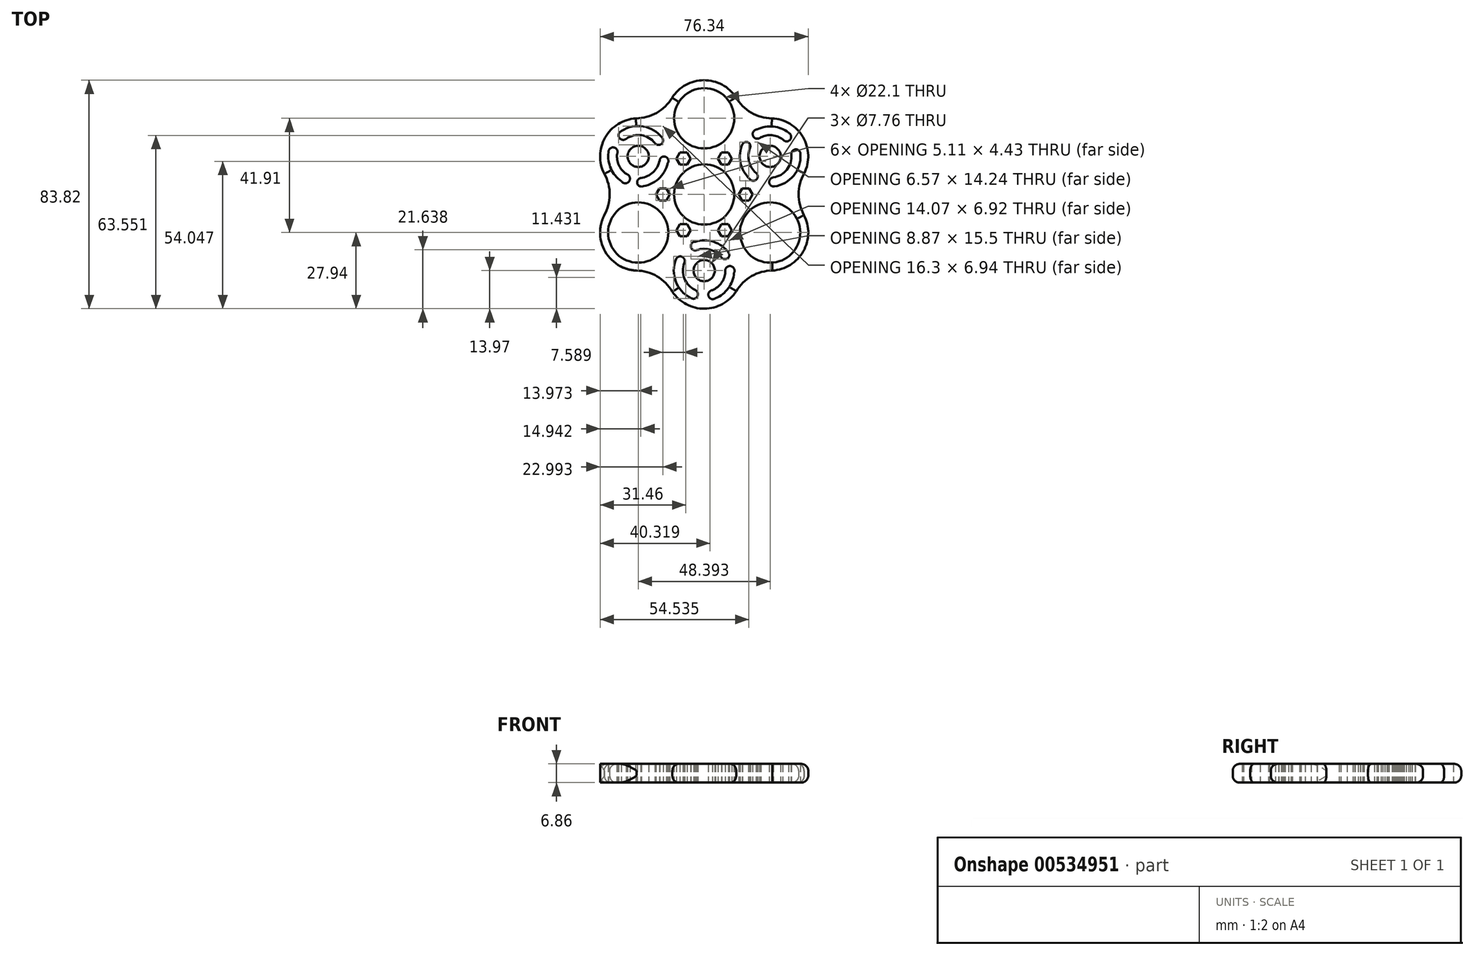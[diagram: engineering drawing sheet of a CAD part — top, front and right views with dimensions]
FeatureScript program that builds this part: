
annotation { "Feature Type Name" : "Feature", "Feature Type Description" : "" }
export const myFeature = defineFeature(function(context is Context, id is Id, definition is map)
    precondition{}
    {
        {
            var Q0;
            Q0=qCreatedBy(makeId("Top.planeOp"),FACE);
            var sketch = newSketch(context, id + "F0", { "sketchPlane" : qUnion([Q0])});
            skCircle(sketch, "E0", {"center": v(0, 0) * mm, "radius": 11.05 * mm});
            skCircle(sketch, "E1", {"center": v(0, 27.94) * mm, "radius": 11.05 * mm});
            skCircle(sketch, "E2.1.0", {"center": v(-24.2, -13.97) * mm, "radius": 11.05 * mm});
            skCircle(sketch, "E2.2.0", {"center": v(24.2, -13.97) * mm, "radius": 11.05 * mm});
            skArc(sketch, "E3", {"start": v(12.1, 34.92) * mm, "mid": v(0.09, 41.9) * mm, "end": v(-12.01, 35.07) * mm});
            skArc(sketch, "E4.1.0", {"start": v(-36.3, -6.98) * mm, "mid": v(-36.34, -20.88) * mm, "end": v(-24.37, -27.94) * mm});
            skArc(sketch, "E4.2.0", {"start": v(24.2, -27.94) * mm, "mid": v(36.25, -21.03) * mm, "end": v(36.38, -7.13) * mm});
            skArc(sketch, "E5.1.0", {"start": v(-24.2, 27.94) * mm, "mid": v(-36.25, 21.03) * mm, "end": v(-36.38, 7.13) * mm});
            skArc(sketch, "E5.3.0", {"start": v(-12.1, -34.92) * mm, "mid": v(-0.09, -41.9) * mm, "end": v(12.01, -35.07) * mm});
            skArc(sketch, "E5.5.0", {"start": v(36.3, 6.98) * mm, "mid": v(36.34, 20.88) * mm, "end": v(24.37, 27.94) * mm});
            skArc(sketch, "E6", {"start": v(-25.03, 27.92) * mm, "mid": v(-17.4, 29.95) * mm, "end": v(-11.76, 35.48) * mm});
            skArc(sketch, "E7.1.0", {"start": v(-36.69, -7.72) * mm, "mid": v(-34.64, -0.1) * mm, "end": v(-36.6, 7.55) * mm});
            skArc(sketch, "E7.2.0", {"start": v(-11.66, -35.63) * mm, "mid": v(-17.23, -30.04) * mm, "end": v(-24.84, -27.93) * mm});
            skArc(sketch, "E7.3.0", {"start": v(25.03, -27.92) * mm, "mid": v(17.4, -29.95) * mm, "end": v(11.76, -35.48) * mm});
            skArc(sketch, "E7.4.0", {"start": v(36.69, 7.72) * mm, "mid": v(34.64, 0.1) * mm, "end": v(36.6, -7.55) * mm});
            skArc(sketch, "E7.5.0", {"start": v(11.66, 35.63) * mm, "mid": v(17.23, 30.04) * mm, "end": v(24.84, 27.93) * mm});
            skCircle(sketch, "E8", {"center": v(-24.2, 13.97) * mm, "radius": 3.88 * mm});
            skArc(sketch, "E9", {"start": v(-15.41, 20.83) * mm, "mid": v(-22.4, 24.97) * mm, "end": v(-30.34, 23.27) * mm});
            skArc(sketch, "E10", {"start": v(-18.06, 18.84) * mm, "mid": v(-23.04, 21.71) * mm, "end": v(-28.64, 20.42) * mm});
            skArc(sketch, "E11", {"start": v(-18.06, 18.84) * mm, "mid": v(-15.73, 18.48) * mm, "end": v(-15.41, 20.83) * mm});
            skArc(sketch, "E12", {"start": v(-30.34, 23.27) * mm, "mid": v(-31.15, 20.85) * mm, "end": v(-28.64, 20.42) * mm});
            skArc(sketch, "E13.1.0", {"start": v(-10.33, -23.76) * mm, "mid": v(-10.42, -31.88) * mm, "end": v(-4.98, -37.9) * mm});
            skArc(sketch, "E13.1.1", {"start": v(-7.28, -25.06) * mm, "mid": v(-7.28, -30.81) * mm, "end": v(-3.36, -35.01) * mm});
            skArc(sketch, "E13.1.2", {"start": v(-7.28, -25.06) * mm, "mid": v(-8.14, -22.86) * mm, "end": v(-10.33, -23.76) * mm});
            skArc(sketch, "E13.1.3", {"start": v(-4.98, -37.9) * mm, "mid": v(-2.48, -37.4) * mm, "end": v(-3.36, -35.01) * mm});
            skArc(sketch, "E13.2.0", {"start": v(25.74, 2.93) * mm, "mid": v(32.82, 6.91) * mm, "end": v(35.32, 14.64) * mm});
            skArc(sketch, "E13.2.1", {"start": v(25.34, 6.22) * mm, "mid": v(30.33, 9.1) * mm, "end": v(32, 14.6) * mm});
            skArc(sketch, "E13.2.2", {"start": v(25.34, 6.22) * mm, "mid": v(23.87, 4.38) * mm, "end": v(25.74, 2.93) * mm});
            skArc(sketch, "E13.2.3", {"start": v(35.32, 14.64) * mm, "mid": v(33.64, 16.55) * mm, "end": v(32, 14.6) * mm});
            skArc(sketch, "E14", {"start": v(-13.35, 11.48) * mm, "mid": v(-16.82, 5.64) * mm, "end": v(-23.02, 2.9) * mm});
            skArc(sketch, "E15", {"start": v(-16.34, 12.55) * mm, "mid": v(-18.73, 8.15) * mm, "end": v(-23.28, 6.04) * mm});
            skArc(sketch, "E16", {"start": v(-30.43, 4.93) * mm, "mid": v(-34.24, 9.53) * mm, "end": v(-35.08, 15.45) * mm});
            skArc(sketch, "E17", {"start": v(-28.52, 7.5) * mm, "mid": v(-31.27, 10.72) * mm, "end": v(-31.92, 14.9) * mm});
            skArc(sketch, "E18", {"start": v(-31.92, 14.9) * mm, "mid": v(-33.13, 17.25) * mm, "end": v(-35.08, 15.45) * mm});
            skArc(sketch, "E19", {"start": v(-30.43, 4.93) * mm, "mid": v(-27.57, 4.8) * mm, "end": v(-28.52, 7.5) * mm});
            skArc(sketch, "E20", {"start": v(-23.28, 6.04) * mm, "mid": v(-24.58, 4.35) * mm, "end": v(-23.02, 2.9) * mm});
            skArc(sketch, "E21", {"start": v(-13.35, 11.48) * mm, "mid": v(-14.19, 13.83) * mm, "end": v(-16.34, 12.55) * mm});
            skArc(sketch, "E22.1.0", {"start": v(7.77, -28.45) * mm, "mid": v(6.35, -32.44) * mm, "end": v(3.06, -35.1) * mm});
            skArc(sketch, "E22.1.1", {"start": v(3.06, -35.1) * mm, "mid": v(1.63, -37.32) * mm, "end": v(4.16, -38.1) * mm});
            skArc(sketch, "E22.1.2", {"start": v(10.94, -28.81) * mm, "mid": v(8.86, -34.42) * mm, "end": v(4.16, -38.1) * mm});
            skArc(sketch, "E22.1.3", {"start": v(10.94, -28.81) * mm, "mid": v(9.63, -26.28) * mm, "end": v(7.77, -28.45) * mm});
            skArc(sketch, "E22.1.4", {"start": v(6.41, -23.18) * mm, "mid": v(8.52, -23.46) * mm, "end": v(9, -21.4) * mm});
            skArc(sketch, "E22.1.5", {"start": v(-2.7, -20.43) * mm, "mid": v(2.31, -20.3) * mm, "end": v(6.41, -23.18) * mm});
            skArc(sketch, "E22.1.6", {"start": v(-3.26, -17.3) * mm, "mid": v(-4.89, -19.2) * mm, "end": v(-2.7, -20.43) * mm});
            skArc(sketch, "E22.1.7", {"start": v(-3.26, -17.3) * mm, "mid": v(3.52, -17.38) * mm, "end": v(9, -21.4) * mm});
            skArc(sketch, "E22.2.0", {"start": v(20.75, 20.95) * mm, "mid": v(24.91, 21.72) * mm, "end": v(28.86, 20.2) * mm});
            skArc(sketch, "E22.2.1", {"start": v(28.86, 20.2) * mm, "mid": v(31.5, 20.07) * mm, "end": v(30.92, 22.65) * mm});
            skArc(sketch, "E22.2.2", {"start": v(19.48, 23.89) * mm, "mid": v(25.38, 24.89) * mm, "end": v(30.92, 22.65) * mm});
            skArc(sketch, "E22.2.3", {"start": v(19.48, 23.89) * mm, "mid": v(17.94, 21.47) * mm, "end": v(20.75, 20.95) * mm});
            skArc(sketch, "E22.2.4", {"start": v(16.87, 17.15) * mm, "mid": v(16.06, 19.1) * mm, "end": v(14.03, 18.49) * mm});
            skArc(sketch, "E22.2.5", {"start": v(19.04, 7.87) * mm, "mid": v(16.42, 12.15) * mm, "end": v(16.87, 17.15) * mm});
            skArc(sketch, "E22.2.6", {"start": v(16.62, 5.83) * mm, "mid": v(19.07, 5.37) * mm, "end": v(19.04, 7.87) * mm});
            skArc(sketch, "E22.2.7", {"start": v(16.62, 5.83) * mm, "mid": v(13.3, 11.74) * mm, "end": v(14.03, 18.49) * mm});
            skCircle(sketch, "E23.1.0", {"center": v(0, -27.94) * mm, "radius": 3.88 * mm});
            skCircle(sketch, "E23.2.0", {"center": v(24.2, 13.97) * mm, "radius": 3.88 * mm});
            skCircle(sketch, "E24.cCircle", {"center": v(15.18, 0) * mm, "radius": 2.21 * mm, "construction": true});
            skLineSegment(sketch, "E24.0", {"start": v(16.46, -2.21) * mm, "end": v(13.9, -2.21) * mm});
            skLineSegment(sketch, "E24.1", {"start": v(13.9, -2.21) * mm, "end": v(12.62, 0) * mm});
            skLineSegment(sketch, "E24.2", {"start": v(12.62, 0) * mm, "end": v(13.9, 2.21) * mm});
            skLineSegment(sketch, "E24.3", {"start": v(13.9, 2.21) * mm, "end": v(16.46, 2.21) * mm});
            skLineSegment(sketch, "E24.4", {"start": v(16.46, 2.21) * mm, "end": v(17.73, 0) * mm});
            skLineSegment(sketch, "E24.5", {"start": v(17.73, 0) * mm, "end": v(16.46, -2.21) * mm});
            skPoint(sketch, "E24.0.midPoint", {"position": v(15.18, -2.21) * mm});
            skLineSegment(sketch, "E25.1.0", {"start": v(8.87, 15.36) * mm, "end": v(10.15, 13.14) * mm});
            skLineSegment(sketch, "E25.1.1", {"start": v(6.31, 15.36) * mm, "end": v(8.87, 15.36) * mm});
            skLineSegment(sketch, "E25.1.2", {"start": v(6.31, 10.93) * mm, "end": v(5.03, 13.14) * mm});
            skLineSegment(sketch, "E25.1.3", {"start": v(5.03, 13.14) * mm, "end": v(6.31, 15.36) * mm});
            skLineSegment(sketch, "E25.1.4", {"start": v(8.87, 10.93) * mm, "end": v(6.31, 10.93) * mm});
            skLineSegment(sketch, "E25.1.5", {"start": v(10.15, 13.14) * mm, "end": v(8.87, 10.93) * mm});
            skPoint(sketch, "E25.1.6", {"position": v(9.5, 12.04) * mm});
            skCircle(sketch, "E25.1.7", {"center": v(7.59, 13.14) * mm, "radius": 2.21 * mm, "construction": true});
            skLineSegment(sketch, "E25.2.0", {"start": v(-8.87, 15.36) * mm, "end": v(-6.31, 15.36) * mm});
            skLineSegment(sketch, "E25.2.1", {"start": v(-10.15, 13.14) * mm, "end": v(-8.87, 15.36) * mm});
            skLineSegment(sketch, "E25.2.2", {"start": v(-6.31, 10.93) * mm, "end": v(-8.87, 10.93) * mm});
            skLineSegment(sketch, "E25.2.3", {"start": v(-8.87, 10.93) * mm, "end": v(-10.15, 13.14) * mm});
            skLineSegment(sketch, "E25.2.4", {"start": v(-5.03, 13.14) * mm, "end": v(-6.31, 10.93) * mm});
            skLineSegment(sketch, "E25.2.5", {"start": v(-6.31, 15.36) * mm, "end": v(-5.03, 13.14) * mm});
            skPoint(sketch, "E25.2.6", {"position": v(-5.67, 14.25) * mm});
            skCircle(sketch, "E25.2.7", {"center": v(-7.59, 13.14) * mm, "radius": 2.21 * mm, "construction": true});
            skLineSegment(sketch, "E25.3.0", {"start": v(-17.73, 0) * mm, "end": v(-16.46, 2.21) * mm});
            skLineSegment(sketch, "E25.3.1", {"start": v(-16.46, -2.21) * mm, "end": v(-17.73, 0) * mm});
            skLineSegment(sketch, "E25.3.2", {"start": v(-12.62, 0) * mm, "end": v(-13.9, -2.21) * mm});
            skLineSegment(sketch, "E25.3.3", {"start": v(-13.9, -2.21) * mm, "end": v(-16.46, -2.21) * mm});
            skLineSegment(sketch, "E25.3.4", {"start": v(-13.9, 2.21) * mm, "end": v(-12.62, 0) * mm});
            skLineSegment(sketch, "E25.3.5", {"start": v(-16.46, 2.21) * mm, "end": v(-13.9, 2.21) * mm});
            skPoint(sketch, "E25.3.6", {"position": v(-15.18, 2.21) * mm});
            skCircle(sketch, "E25.3.7", {"center": v(-15.18, 0) * mm, "radius": 2.21 * mm, "construction": true});
            skLineSegment(sketch, "E25.4.0", {"start": v(-8.87, -15.36) * mm, "end": v(-10.15, -13.14) * mm});
            skLineSegment(sketch, "E25.4.1", {"start": v(-6.31, -15.36) * mm, "end": v(-8.87, -15.36) * mm});
            skLineSegment(sketch, "E25.4.2", {"start": v(-6.31, -10.93) * mm, "end": v(-5.03, -13.14) * mm});
            skLineSegment(sketch, "E25.4.3", {"start": v(-5.03, -13.14) * mm, "end": v(-6.31, -15.36) * mm});
            skLineSegment(sketch, "E25.4.4", {"start": v(-8.87, -10.93) * mm, "end": v(-6.31, -10.93) * mm});
            skLineSegment(sketch, "E25.4.5", {"start": v(-10.15, -13.14) * mm, "end": v(-8.87, -10.93) * mm});
            skPoint(sketch, "E25.4.6", {"position": v(-9.5, -12.04) * mm});
            skCircle(sketch, "E25.4.7", {"center": v(-7.59, -13.14) * mm, "radius": 2.21 * mm, "construction": true});
            skLineSegment(sketch, "E25.5.0", {"start": v(8.87, -15.36) * mm, "end": v(6.31, -15.36) * mm});
            skLineSegment(sketch, "E25.5.1", {"start": v(10.15, -13.14) * mm, "end": v(8.87, -15.36) * mm});
            skLineSegment(sketch, "E25.5.2", {"start": v(6.31, -10.93) * mm, "end": v(8.87, -10.93) * mm});
            skLineSegment(sketch, "E25.5.3", {"start": v(8.87, -10.93) * mm, "end": v(10.15, -13.14) * mm});
            skLineSegment(sketch, "E25.5.4", {"start": v(5.03, -13.14) * mm, "end": v(6.31, -10.93) * mm});
            skLineSegment(sketch, "E25.5.5", {"start": v(6.31, -15.36) * mm, "end": v(5.03, -13.14) * mm});
            skPoint(sketch, "E25.5.6", {"position": v(5.67, -14.25) * mm});
            skCircle(sketch, "E25.5.7", {"center": v(7.59, -13.14) * mm, "radius": 2.21 * mm, "construction": true});
            skSolve(sketch);
        }
        {
            var Q0;
            Q0=makeQuery(id+"F0.imprint","IMPRINT",FACE,{"disambiguationData":[TD([[makeQuery(id+"F0.imprint","IMPRINT",EDGE,{"derivedFrom":sQuery(id+"F0.wireOp",EDGE,"E0")}),-1.0]])]});
            extrude(context, id + "F1", {"entities" : qUnion([Q0]), "depth" : 6.86 * mm, "offsetDistance" : 25.4 * mm});
        }
        {
            var Q0;
            Q0=makeQuery(id+"F1.opExtrude","CAP_EDGE",EDGE,{"disambiguationData":[OSD([sQuery(id+"F0.wireOp",EDGE,"E6")])],"isStart":true});
            var Q1;
            Q1=makeQuery(id+"F1.opExtrude","CAP_EDGE",EDGE,{"disambiguationData":[OSD([sQuery(id+"F0.wireOp",EDGE,"E3")])],"isStart":true});
            var Q2;
            Q2=makeQuery(id+"F1.opExtrude","CAP_EDGE",EDGE,{"disambiguationData":[OSD([sQuery(id+"F0.wireOp",EDGE,"E7.5.0")])],"isStart":true});
            var Q3;
            Q3=makeQuery(id+"F1.opExtrude","CAP_EDGE",EDGE,{"disambiguationData":[OSD([sQuery(id+"F0.wireOp",EDGE,"E5.5.0")])],"isStart":true});
            var Q4;
            Q4=makeQuery(id+"F1.opExtrude","CAP_EDGE",EDGE,{"disambiguationData":[OSD([sQuery(id+"F0.wireOp",EDGE,"E7.4.0")])],"isStart":true});
            var Q5;
            Q5=makeQuery(id+"F1.opExtrude","CAP_EDGE",EDGE,{"disambiguationData":[OSD([sQuery(id+"F0.wireOp",EDGE,"E4.2.0")])],"isStart":true});
            var Q6;
            Q6=makeQuery(id+"F1.opExtrude","CAP_EDGE",EDGE,{"disambiguationData":[OSD([sQuery(id+"F0.wireOp",EDGE,"E7.3.0")])],"isStart":true});
            var Q7;
            Q7=makeQuery(id+"F1.opExtrude","CAP_EDGE",EDGE,{"disambiguationData":[OSD([sQuery(id+"F0.wireOp",EDGE,"E5.3.0")])],"isStart":true});
            var Q8;
            Q8=makeQuery(id+"F1.opExtrude","CAP_EDGE",EDGE,{"disambiguationData":[OSD([sQuery(id+"F0.wireOp",EDGE,"E7.2.0")])],"isStart":true});
            var Q9;
            Q9=makeQuery(id+"F1.opExtrude","CAP_EDGE",EDGE,{"disambiguationData":[OSD([sQuery(id+"F0.wireOp",EDGE,"E4.1.0")])],"isStart":true});
            var Q10;
            Q10=makeQuery(id+"F1.opExtrude","CAP_EDGE",EDGE,{"disambiguationData":[OSD([sQuery(id+"F0.wireOp",EDGE,"E7.1.0")])],"isStart":true});
            var Q11;
            Q11=makeQuery(id+"F1.opExtrude","CAP_EDGE",EDGE,{"disambiguationData":[OSD([sQuery(id+"F0.wireOp",EDGE,"E5.1.0")])],"isStart":true});
            var Q12;
            Q12=makeQuery(id+"F1.opExtrude","CAP_EDGE",EDGE,{"disambiguationData":[OSD([sQuery(id+"F0.wireOp",EDGE,"E7.2.0")])],"isStart":false});
            var Q13;
            Q13=makeQuery(id+"F1.opExtrude","CAP_EDGE",EDGE,{"disambiguationData":[OSD([sQuery(id+"F0.wireOp",EDGE,"E5.3.0")])],"isStart":false});
            var Q14;
            Q14=makeQuery(id+"F1.opExtrude","CAP_EDGE",EDGE,{"disambiguationData":[OSD([sQuery(id+"F0.wireOp",EDGE,"E4.1.0")])],"isStart":false});
            var Q15;
            Q15=makeQuery(id+"F1.opExtrude","CAP_EDGE",EDGE,{"disambiguationData":[OSD([sQuery(id+"F0.wireOp",EDGE,"E7.1.0")])],"isStart":false});
            var Q16;
            Q16=makeQuery(id+"F1.opExtrude","CAP_EDGE",EDGE,{"disambiguationData":[OSD([sQuery(id+"F0.wireOp",EDGE,"E5.1.0")])],"isStart":false});
            var Q17;
            Q17=makeQuery(id+"F1.opExtrude","CAP_EDGE",EDGE,{"disambiguationData":[OSD([sQuery(id+"F0.wireOp",EDGE,"E6")])],"isStart":false});
            var Q18;
            Q18=makeQuery(id+"F1.opExtrude","CAP_EDGE",EDGE,{"disambiguationData":[OSD([sQuery(id+"F0.wireOp",EDGE,"E3")])],"isStart":false});
            var Q19;
            Q19=makeQuery(id+"F1.opExtrude","CAP_EDGE",EDGE,{"disambiguationData":[OSD([sQuery(id+"F0.wireOp",EDGE,"E7.5.0")])],"isStart":false});
            var Q20;
            Q20=makeQuery(id+"F1.opExtrude","CAP_EDGE",EDGE,{"disambiguationData":[OSD([sQuery(id+"F0.wireOp",EDGE,"E7.3.0")])],"isStart":false});
            var Q21;
            Q21=makeQuery(id+"F1.opExtrude","CAP_EDGE",EDGE,{"disambiguationData":[OSD([sQuery(id+"F0.wireOp",EDGE,"E4.2.0")])],"isStart":false});
            var Q22;
            Q22=makeQuery(id+"F1.opExtrude","CAP_EDGE",EDGE,{"disambiguationData":[OSD([sQuery(id+"F0.wireOp",EDGE,"E7.4.0")])],"isStart":false});
            var Q23;
            Q23=makeQuery(id+"F1.opExtrude","CAP_EDGE",EDGE,{"disambiguationData":[OSD([sQuery(id+"F0.wireOp",EDGE,"E5.5.0")])],"isStart":false});
            fillet(context, id + "F2", {"entities" : qUnion([Q0, Q1, Q2, Q3, Q4, Q5, Q6, Q7, Q8, Q9, Q10, Q11, Q12, Q13, Q14, Q15, Q16, Q17, Q18, Q19, Q20, Q21, Q22, Q23]), "radius" : 2.54 * mm, "tangentPropagation" : true, "allowEdgeOverflow" : false});
        }
    });
